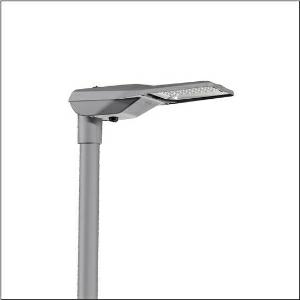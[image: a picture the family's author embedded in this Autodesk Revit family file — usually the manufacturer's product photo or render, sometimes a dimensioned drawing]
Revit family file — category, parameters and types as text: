
# Revit family: streetlight_sl_21_mini___p0_5a_5xe2v33t08jb_709b
name_source: partatom
category: Lighting Fixtures
units: mm (PartAtom-declared; Revit-internal decimal feet)

## family parameters
Cut with Voids When Loaded = No
Host = Face
Light Source = No
Part Type = Normal
Room Calculation Point = No
Round Connector Dimension = Use Diameter
Shared = No

## types (1)
- --- (1 x LED, 12720 lm, 88.6 W, 3000K)
    Apparent Load = 89 VA
    CIE Flux Codes = 37 73 96 100 100
    Color Rendering = 70
    Color Temperature = 3000K
    Default Elevation = 1800 mm
    Description = Streetlight SL 21 mini, mast luminaire, primary light control with lens, of PMMA, primary optical cover: cover, of toughened safety glass, transparent, light distribution: P0.5a, light emission: direct distribution, primary light characteristic: asymmetric, installation type: post-top, side-entry, LED, High Power LED, rated luminous flux: 12.720lm, luminous efficacy: 144lm/W, light colour: 730, colour temperature: 3000K, control gear: D4i, control: pre-setting: logarithmic dimming characteristic, flexible luminous flux parameterisation, time-dependent luminous flux control, constant luminous flux control, overheat protection, mains connection: 220..240V, AC, 50/60Hz, start of lifetime: 89W, end of service life: 92W, reduction: 41W, luminaire housing, of diecast aluminium, powder-coated, SITECO metallic grey (DB 702S), corrosivity category C5 high according to DIN EN ISO 12944, multi-level sealing system, sealing non-destructively replaceable, inclination adjustable: 0°, 5°, 10°, 15°, please order mast flange separately, length: 628mm, width: 235mm, height: 110mm, mast flange for spigot size: 42mm (side-entry): 5XC10008XM4, 60/48mm (side-entry/post-top): 5XC10108XM2, 76/60mm (side-entry/post-top): 5XC10108XM1, mounting height: 4..8m, Smart Interface below and above, protection rating (complete): IP66, insulation class (complete): insulation class II (safety insulation), certification: CE, ENEC, ENEC+, VDE, impact resistance: IK10, permissible operating ambient temperature for outdoor applications: -40..+50°C, standard-compliant lighting for roads and squares, packaging unit: 1 piece

Light Distribution: P0.5a
    Height = 110 mm
    Lamp = 1 x LED
    Lamp Light Flux = 12720 lm
    Lamp Power = 88.6 W
    Lamp count = 1
    Length = 625 mm
    Luminous efficacy = 144 lm/W
    Manufacturer = Siteco
    ModVariant = No
    Model = 5XE2V33T08JB
    Number of Poles = 1
    OnlyDefault = Yes
    Power Factor = 1
    Product Name = Streetlight SL 21 mini | P0.5a
    Product group = mast luminaire | pylon top
    ProductGroupID = 6100
    Protection Class = Protection class II
    Protection Degree = IP 66
    RLX_Detail_Level = 1
    RLX_Emergency_Light_Flux = 0 lm
    RLX_Emergency_Type = 0
    RLX_Emergency_Type_DB = No
    RlxData = <blob elided: 26137 chars, md5=247abc4b>
    Socket = socket
    Standby Power = 0 W
    System Light Flux = 12720 lm
    System Power = 89 W
    Type Comments = factory setting: luminous flux: 100 % | dim-lin: 254 | 915 mA
    Type Image = l_1003514.jpg
    URL = http://relux.com
    VarID = @adj_032697
    Voltage = 0 V
    Weight = 0.00 kg
    Width = 234 mm

## geometry (parser evidence)
native form markers: Blend x4, Sweep x11
no freeform markers — native parametric forms only
